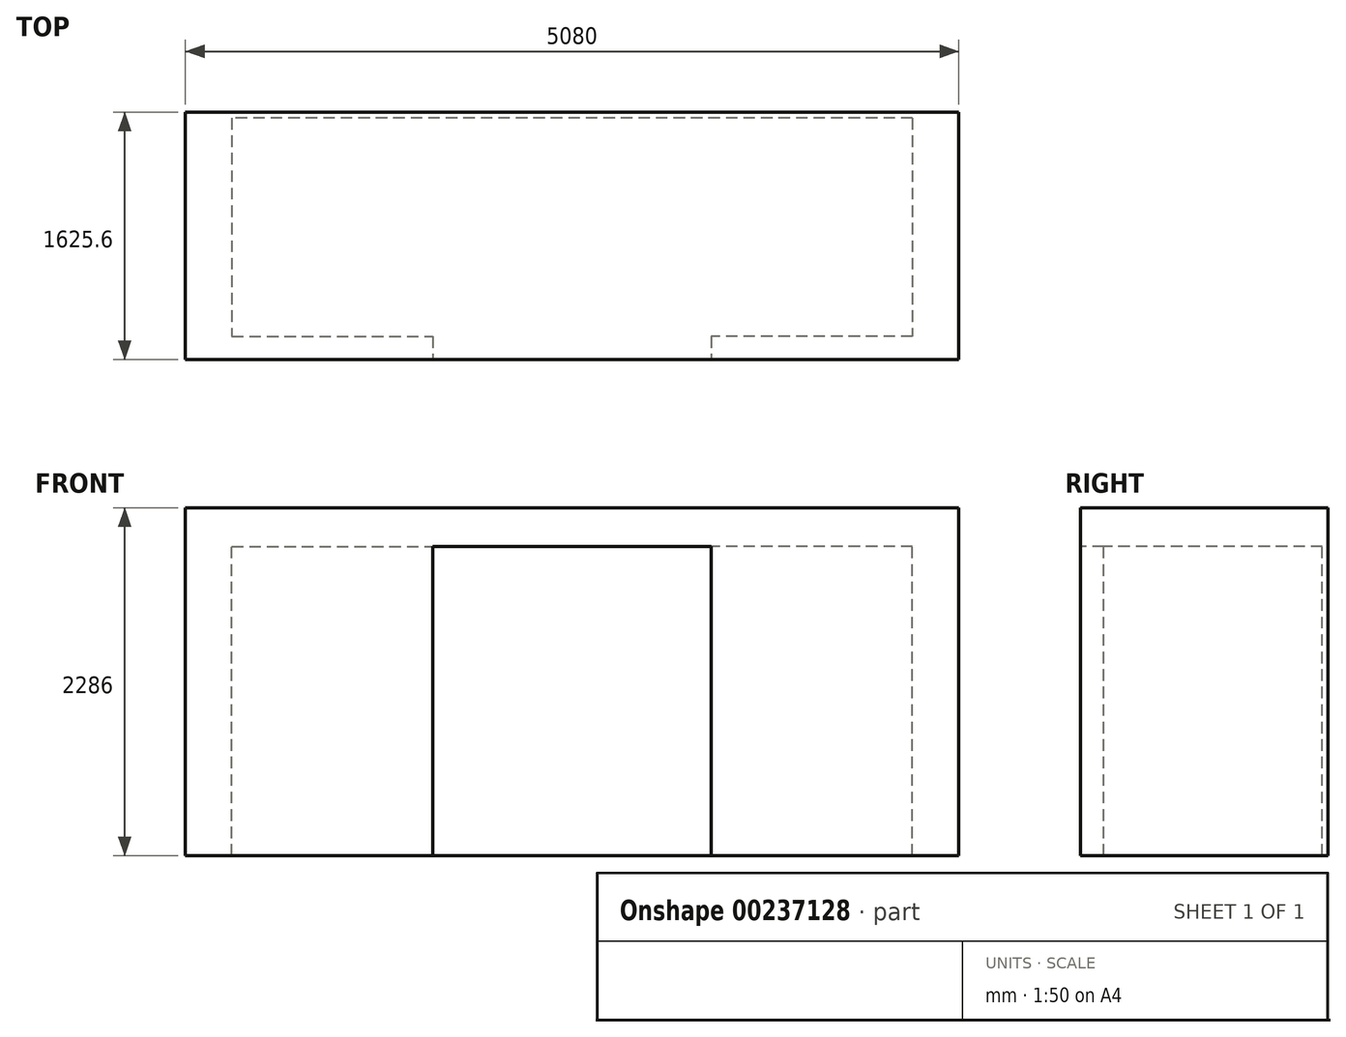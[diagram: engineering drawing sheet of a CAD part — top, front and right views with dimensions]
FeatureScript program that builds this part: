
annotation { "Feature Type Name" : "Feature", "Feature Type Description" : "" }
export const myFeature = defineFeature(function(context is Context, id is Id, definition is map)
    precondition{}
    {
        {
            var Q0;
            Q0=qCreatedBy(makeId("Top.planeOp"),FACE);
            var sketch = newSketch(context, id + "F0", { "sketchPlane" : qUnion([Q0])});
            skLineSegment(sketch, "E0.bottom", {"start": v(2540, -812.8) * mm, "end": v(-2540, -812.8) * mm});
            skLineSegment(sketch, "E0.top", {"start": v(2540, 812.8) * mm, "end": v(-2540, 812.8) * mm});
            skLineSegment(sketch, "E0.left", {"start": v(2540, -812.8) * mm, "end": v(2540, 812.8) * mm});
            skLineSegment(sketch, "E0.right", {"start": v(-2540, -812.8) * mm, "end": v(-2540, 812.8) * mm});
            skPoint(sketch, "E0.middle", {"position": v(0, 0) * mm});
            skSolve(sketch);
        }
        {
            var Q0;
            Q0=makeQuery(id+"F0.imprint","IMPRINT",FACE,{"disambiguationData":[TD([[makeQuery(id+"F0.imprint","IMPRINT",EDGE,{"derivedFrom":sQuery(id+"F0.wireOp",EDGE,"E0.bottom")}),-1.0]])]});
            extrude(context, id + "F1", {"entities" : qUnion([Q0]), "depth" : 2286 * mm});
        }
        {
            var Q0;
            Q0=makeQuery(id+"F1.opExtrude","SWEPT_FACE",FACE,{"disambiguationData":[OSD([sQuery(id+"F0.wireOp",EDGE,"E0.bottom")])]});
            var sketch = newSketch(context, id + "F2", { "sketchPlane" : qUnion([Q0])});
            skLineSegment(sketch, "E1.bottom", {"start": v(914.4, 0) * mm, "end": v(-914.4, 0) * mm});
            skLineSegment(sketch, "E1.top", {"start": v(914.4, 2032) * mm, "end": v(-914.4, 2032) * mm});
            skLineSegment(sketch, "E1.left", {"start": v(914.4, 0) * mm, "end": v(914.4, 2032) * mm});
            skLineSegment(sketch, "E1.right", {"start": v(-914.4, 0) * mm, "end": v(-914.4, 2032) * mm});
            skSolve(sketch);
        }
        {
            var Q0;
            Q0=makeQuery(id+"F2.imprint","IMPRINT",FACE,{"disambiguationData":[TD([[makeQuery(id+"F2.imprint","IMPRINT",EDGE,{"derivedFrom":sQuery(id+"F2.wireOp",EDGE,"E1.bottom")}),-1.0]])]});
            extrude(context, id + "F3", {"entities" : qUnion([Q0]), "operationType" : NewBodyOperationType.REMOVE, "oppositeDirection" : true, "depth" : 1587.5 * mm});
        }
        {
            var Q0;
            Q0=makeQuery(id+"F3.boolean.opBoolean","COPY",FACE,{"derivedFrom":makeQuery(id+"F3.opExtrude","SWEPT_FACE",FACE,{"disambiguationData":[OSD([sQuery(id+"F2.wireOp",EDGE,"E1.left")])]})});
            var sketch = newSketch(context, id + "F4", { "sketchPlane" : qUnion([Q0])});
            skLineSegment(sketch, "E2.bottom", {"start": v(-774.7, 0) * mm, "end": v(660.4, 0) * mm});
            skLineSegment(sketch, "E2.top", {"start": v(-774.7, 2032) * mm, "end": v(660.4, 2032) * mm});
            skLineSegment(sketch, "E2.left", {"start": v(-774.7, 0) * mm, "end": v(-774.7, 2032) * mm});
            skLineSegment(sketch, "E2.right", {"start": v(660.4, 0) * mm, "end": v(660.4, 2032) * mm});
            skSolve(sketch);
        }
        {
            var Q0;
            Q0=makeQuery(id+"F4.imprint","IMPRINT",FACE,{"disambiguationData":[TD([[makeQuery(id+"F4.imprint","IMPRINT",EDGE,{"derivedFrom":sQuery(id+"F4.wireOp",EDGE,"E2.bottom")}),1.0]])]});
            extrude(context, id + "F5", {"entities" : qUnion([Q0]), "operationType" : NewBodyOperationType.REMOVE, "oppositeDirection" : true, "depth" : 1320.8 * mm});
        }
        {
            var Q0;
            Q0=makeQuery(id+"F3.boolean.opBoolean","COPY",FACE,{"derivedFrom":makeQuery(id+"F3.opExtrude","SWEPT_FACE",FACE,{"disambiguationData":[OSD([sQuery(id+"F2.wireOp",EDGE,"E1.right")])]})});
            var sketch = newSketch(context, id + "F6", { "sketchPlane" : qUnion([Q0])});
            skLineSegment(sketch, "E3.bottom", {"start": v(774.7, 0) * mm, "end": v(-660.4, 0) * mm});
            skLineSegment(sketch, "E3.top", {"start": v(774.7, 2032) * mm, "end": v(-660.4, 2032) * mm});
            skLineSegment(sketch, "E3.left", {"start": v(774.7, 0) * mm, "end": v(774.7, 2032) * mm});
            skLineSegment(sketch, "E3.right", {"start": v(-660.4, 0) * mm, "end": v(-660.4, 2032) * mm});
            skSolve(sketch);
        }
        {
            var Q0;
            Q0=makeQuery(id+"F6.imprint","IMPRINT",FACE,{"disambiguationData":[TD([[makeQuery(id+"F6.imprint","IMPRINT",EDGE,{"derivedFrom":sQuery(id+"F6.wireOp",EDGE,"E3.bottom")}),-1.0]])]});
            extrude(context, id + "F7", {"entities" : qUnion([Q0]), "operationType" : NewBodyOperationType.REMOVE, "oppositeDirection" : true, "depth" : 1320.8 * mm});
        }
    });
